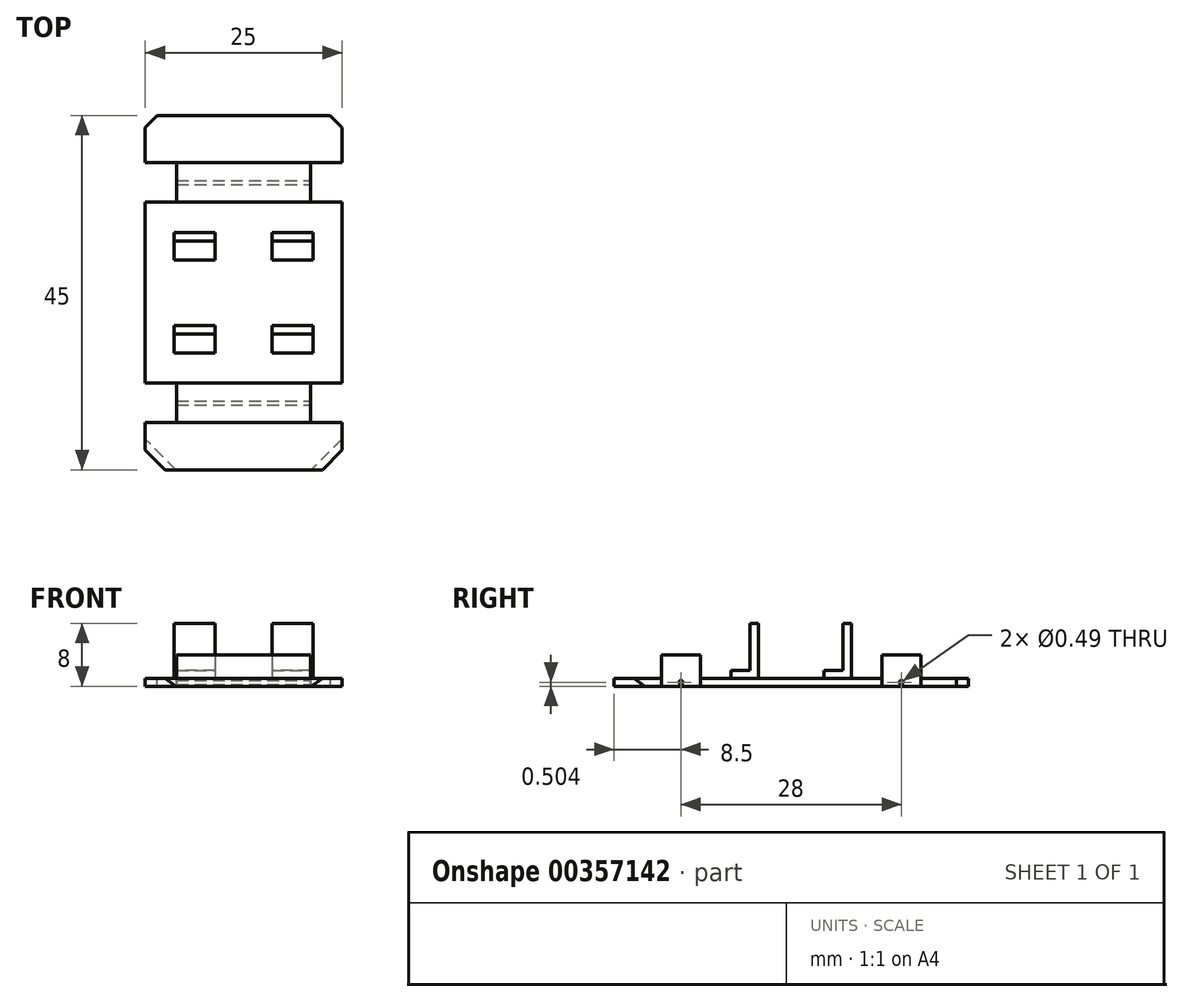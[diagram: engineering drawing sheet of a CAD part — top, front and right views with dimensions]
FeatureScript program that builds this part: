
annotation { "Feature Type Name" : "Feature", "Feature Type Description" : "" }
export const myFeature = defineFeature(function(context is Context, id is Id, definition is map)
    precondition{}
    {
        {
            var Q0;
            Q0=qCreatedBy(makeId("Top.planeOp"),FACE);
            var sketch = newSketch(context, id + "F0", { "sketchPlane" : qUnion([Q0])});
            skLineSegment(sketch, "E0.bottom", {"start": v(12.5, -22.5) * mm, "end": v(-12.5, -22.5) * mm});
            skLineSegment(sketch, "E0.top", {"start": v(12.5, 22.5) * mm, "end": v(-12.5, 22.5) * mm});
            skLineSegment(sketch, "E0.left", {"start": v(12.5, -22.5) * mm, "end": v(12.5, -16.5) * mm});
            skLineSegment(sketch, "E0.right", {"start": v(-12.5, -22.5) * mm, "end": v(-12.5, -16.5) * mm});
            skPoint(sketch, "E0.middle", {"position": v(0, 0) * mm});
            skLineSegment(sketch, "E1.bottom", {"start": v(-12.5, 16.5) * mm, "end": v(-8.5, 16.5) * mm});
            skLineSegment(sketch, "E1.top", {"start": v(-12.5, 11.5) * mm, "end": v(-8.5, 11.5) * mm});
            skLineSegment(sketch, "E1.right", {"start": v(-8.5, 16.5) * mm, "end": v(-8.5, 11.5) * mm});
            skLineSegment(sketch, "E2.MirrorCS", {"start": v(8.5, 16.5) * mm, "end": v(8.5, 11.5) * mm});
            skLineSegment(sketch, "E3.MirrorCS", {"start": v(12.5, 16.5) * mm, "end": v(8.5, 16.5) * mm});
            skLineSegment(sketch, "E4.MirrorCS", {"start": v(12.5, 11.5) * mm, "end": v(8.5, 11.5) * mm});
            skLineSegment(sketch, "E5.MirrorCS", {"start": v(12.5, -11.5) * mm, "end": v(8.5, -11.5) * mm});
            skLineSegment(sketch, "E6.MirrorCS", {"start": v(8.5, -16.5) * mm, "end": v(8.5, -11.5) * mm});
            skLineSegment(sketch, "E7.MirrorCS", {"start": v(12.5, -16.5) * mm, "end": v(8.5, -16.5) * mm});
            skLineSegment(sketch, "E8.MirrorCS", {"start": v(-12.5, -11.5) * mm, "end": v(-8.5, -11.5) * mm});
            skLineSegment(sketch, "E9.MirrorCS", {"start": v(-8.5, -16.5) * mm, "end": v(-8.5, -11.5) * mm});
            skLineSegment(sketch, "E10.MirrorCS", {"start": v(-12.5, -16.5) * mm, "end": v(-8.5, -16.5) * mm});
            skLineSegment(sketch, "E11.trimOffspring", {"start": v(12.5, 16.5) * mm, "end": v(12.5, 22.5) * mm});
            skLineSegment(sketch, "E12.trimOffspring", {"start": v(-12.5, 16.5) * mm, "end": v(-12.5, 22.5) * mm});
            skLineSegment(sketch, "E13.trimOffspring", {"start": v(-12.5, -11.5) * mm, "end": v(-12.5, 11.5) * mm});
            skLineSegment(sketch, "E14.trimOffspring", {"start": v(12.5, -11.5) * mm, "end": v(12.5, 11.5) * mm});
            skSolve(sketch);
        }
        {
            var Q0;
            Q0 = qSketchRegion(id + "F0", true);
            extrude(context, id + "F1", {"entities" : qUnion([Q0]), "depth" : 1 * mm});
        }
        {
            var Q0;
            Q0=qCreatedBy(makeId("Right.planeOp"),FACE);
            var sketch = newSketch(context, id + "F2", { "sketchPlane" : qUnion([Q0])});
            skLineSegment(sketch, "E15", {"start": v(-16.5, 1) * mm, "end": v(-11.5, 1) * mm});
            skPoint(sketch, "E16.centerSnap0", {"position": v(-14, 1) * mm});
            skLineSegment(sketch, "E17.MirrorCS", {"start": v(16.5, 1) * mm, "end": v(11.5, 1) * mm});
            skLineSegment(sketch, "E18.top", {"start": v(-16.5, 4) * mm, "end": v(-11.5, 4) * mm});
            skLineSegment(sketch, "E18.left", {"start": v(-16.5, 1) * mm, "end": v(-16.5, 4) * mm});
            skLineSegment(sketch, "E18.right", {"start": v(-11.5, 1) * mm, "end": v(-11.5, 4) * mm});
            skLineSegment(sketch, "E19.bottom", {"start": v(11.5, 1) * mm, "end": v(16.5, 1) * mm});
            skLineSegment(sketch, "E19.top", {"start": v(11.5, 4) * mm, "end": v(16.5, 4) * mm});
            skLineSegment(sketch, "E19.left", {"start": v(11.5, 1) * mm, "end": v(11.5, 4) * mm});
            skLineSegment(sketch, "E19.right", {"start": v(16.5, 1) * mm, "end": v(16.5, 4) * mm});
            skPoint(sketch, "E20.centerSnap0", {"position": v(14, 1) * mm});
            skSolve(sketch);
        }
        {
            var Q0;
            Q0 = qSketchRegion(id + "F2", true);
            extrude(context, id + "F3", {"entities" : qUnion([Q0]), "operationType" : NewBodyOperationType.ADD, "endBound" : BoundingType.SYMMETRIC, "depth" : 17 * mm});
        }
        {
            var Q0;
            Q0=makeQuery(id+"F1.opExtrude","SWEPT_EDGE",EDGE,{"disambiguationData":[OSD([sQuery(id+"F0.wireOp",EDGE,"E0.bottom"),sQuery(id+"F0.wireOp",EDGE,"E0.left")])]});
            var Q1;
            Q1=makeQuery(id+"F1.opExtrude","SWEPT_EDGE",EDGE,{"disambiguationData":[OSD([sQuery(id+"F0.wireOp",EDGE,"E0.bottom"),sQuery(id+"F0.wireOp",EDGE,"E0.right")])]});
            chamfer(context, id + "F4", {"entities" : qUnion([Q0, Q1]), "width" : 2.5 * mm, "tangentPropagation" : true});
        }
        {
            var Q0;
            Q0=makeQuery(id+"F1.opExtrude","SWEPT_EDGE",EDGE,{"disambiguationData":[OSD([sQuery(id+"F0.wireOp",EDGE,"E0.top"),sQuery(id+"F0.wireOp",EDGE,"E11.trimOffspring")])]});
            var Q1;
            Q1=makeQuery(id+"F1.opExtrude","SWEPT_EDGE",EDGE,{"disambiguationData":[OSD([sQuery(id+"F0.wireOp",EDGE,"E0.top"),sQuery(id+"F0.wireOp",EDGE,"E12.trimOffspring")])]});
            chamfer(context, id + "F5", {"entities" : qUnion([Q0, Q1]), "width" : 1.5 * mm, "tangentPropagation" : true});
        }
        {
            var Q0;
            {var subQ0=sQuery(id+"F0.wireOp",EDGE,"E0.right");var subQ1=sQuery(id+"F0.wireOp",EDGE,"E0.bottom");Q0=makeQuery(id+"F4.opChamfer","BLEND_EDGE",EDGE,{"blendedFrom":[makeQuery(id+"F1.opExtrude","SWEPT_EDGE",EDGE,{"disambiguationData":[OSD([subQ1,subQ0])]}),makeQuery(id+"F1.opExtrude","CAP_FACE",FACE,{"disambiguationData":[OSD([subQ1,sQuery(id+"F0.wireOp",EDGE,"E0.top"),sQuery(id+"F0.wireOp",EDGE,"E0.left"),subQ0,sQuery(id+"F0.wireOp",EDGE,"E1.bottom"),sQuery(id+"F0.wireOp",EDGE,"E1.top"),sQuery(id+"F0.wireOp",EDGE,"E1.right"),sQuery(id+"F0.wireOp",EDGE,"E2.MirrorCS"),sQuery(id+"F0.wireOp",EDGE,"E3.MirrorCS"),sQuery(id+"F0.wireOp",EDGE,"E4.MirrorCS"),sQuery(id+"F0.wireOp",EDGE,"E5.MirrorCS"),sQuery(id+"F0.wireOp",EDGE,"E6.MirrorCS"),sQuery(id+"F0.wireOp",EDGE,"E7.MirrorCS"),sQuery(id+"F0.wireOp",EDGE,"E8.MirrorCS"),sQuery(id+"F0.wireOp",EDGE,"E9.MirrorCS"),sQuery(id+"F0.wireOp",EDGE,"E10.MirrorCS"),sQuery(id+"F0.wireOp",EDGE,"E11.trimOffspring"),sQuery(id+"F0.wireOp",EDGE,"E12.trimOffspring"),sQuery(id+"F0.wireOp",EDGE,"E13.trimOffspring"),sQuery(id+"F0.wireOp",EDGE,"E14.trimOffspring")])],"isStart":true})],"blendedInto":[makeQuery(id+"F1.opExtrude","CAP_FACE",FACE,{"disambiguationData":[OSD([subQ1,sQuery(id+"F0.wireOp",EDGE,"E0.top"),sQuery(id+"F0.wireOp",EDGE,"E0.left"),subQ0,sQuery(id+"F0.wireOp",EDGE,"E1.bottom"),sQuery(id+"F0.wireOp",EDGE,"E1.top"),sQuery(id+"F0.wireOp",EDGE,"E1.right"),sQuery(id+"F0.wireOp",EDGE,"E2.MirrorCS"),sQuery(id+"F0.wireOp",EDGE,"E3.MirrorCS"),sQuery(id+"F0.wireOp",EDGE,"E4.MirrorCS"),sQuery(id+"F0.wireOp",EDGE,"E5.MirrorCS"),sQuery(id+"F0.wireOp",EDGE,"E6.MirrorCS"),sQuery(id+"F0.wireOp",EDGE,"E7.MirrorCS"),sQuery(id+"F0.wireOp",EDGE,"E8.MirrorCS"),sQuery(id+"F0.wireOp",EDGE,"E9.MirrorCS"),sQuery(id+"F0.wireOp",EDGE,"E10.MirrorCS"),sQuery(id+"F0.wireOp",EDGE,"E11.trimOffspring"),sQuery(id+"F0.wireOp",EDGE,"E12.trimOffspring"),sQuery(id+"F0.wireOp",EDGE,"E13.trimOffspring"),sQuery(id+"F0.wireOp",EDGE,"E14.trimOffspring")])],"isStart":true})]});}
            var Q1;
            {var subQ0=sQuery(id+"F0.wireOp",EDGE,"E0.left");var subQ1=sQuery(id+"F0.wireOp",EDGE,"E0.bottom");Q1=makeQuery(id+"F4.opChamfer","BLEND_EDGE",EDGE,{"blendedFrom":[makeQuery(id+"F1.opExtrude","SWEPT_EDGE",EDGE,{"disambiguationData":[OSD([subQ1,subQ0])]}),makeQuery(id+"F1.opExtrude","CAP_FACE",FACE,{"disambiguationData":[OSD([subQ1,sQuery(id+"F0.wireOp",EDGE,"E0.top"),subQ0,sQuery(id+"F0.wireOp",EDGE,"E0.right"),sQuery(id+"F0.wireOp",EDGE,"E1.bottom"),sQuery(id+"F0.wireOp",EDGE,"E1.top"),sQuery(id+"F0.wireOp",EDGE,"E1.right"),sQuery(id+"F0.wireOp",EDGE,"E2.MirrorCS"),sQuery(id+"F0.wireOp",EDGE,"E3.MirrorCS"),sQuery(id+"F0.wireOp",EDGE,"E4.MirrorCS"),sQuery(id+"F0.wireOp",EDGE,"E5.MirrorCS"),sQuery(id+"F0.wireOp",EDGE,"E6.MirrorCS"),sQuery(id+"F0.wireOp",EDGE,"E7.MirrorCS"),sQuery(id+"F0.wireOp",EDGE,"E8.MirrorCS"),sQuery(id+"F0.wireOp",EDGE,"E9.MirrorCS"),sQuery(id+"F0.wireOp",EDGE,"E10.MirrorCS"),sQuery(id+"F0.wireOp",EDGE,"E11.trimOffspring"),sQuery(id+"F0.wireOp",EDGE,"E12.trimOffspring"),sQuery(id+"F0.wireOp",EDGE,"E13.trimOffspring"),sQuery(id+"F0.wireOp",EDGE,"E14.trimOffspring")])],"isStart":true})],"blendedInto":[makeQuery(id+"F1.opExtrude","CAP_FACE",FACE,{"disambiguationData":[OSD([subQ1,sQuery(id+"F0.wireOp",EDGE,"E0.top"),subQ0,sQuery(id+"F0.wireOp",EDGE,"E0.right"),sQuery(id+"F0.wireOp",EDGE,"E1.bottom"),sQuery(id+"F0.wireOp",EDGE,"E1.top"),sQuery(id+"F0.wireOp",EDGE,"E1.right"),sQuery(id+"F0.wireOp",EDGE,"E2.MirrorCS"),sQuery(id+"F0.wireOp",EDGE,"E3.MirrorCS"),sQuery(id+"F0.wireOp",EDGE,"E4.MirrorCS"),sQuery(id+"F0.wireOp",EDGE,"E5.MirrorCS"),sQuery(id+"F0.wireOp",EDGE,"E6.MirrorCS"),sQuery(id+"F0.wireOp",EDGE,"E7.MirrorCS"),sQuery(id+"F0.wireOp",EDGE,"E8.MirrorCS"),sQuery(id+"F0.wireOp",EDGE,"E9.MirrorCS"),sQuery(id+"F0.wireOp",EDGE,"E10.MirrorCS"),sQuery(id+"F0.wireOp",EDGE,"E11.trimOffspring"),sQuery(id+"F0.wireOp",EDGE,"E12.trimOffspring"),sQuery(id+"F0.wireOp",EDGE,"E13.trimOffspring"),sQuery(id+"F0.wireOp",EDGE,"E14.trimOffspring")])],"isStart":true})]});}
            chamfer(context, id + "F6", {"entities" : qUnion([Q0, Q1]), "width" : 1 * mm, "tangentPropagation" : true});
        }
        {
            var Q0;
            Q0=makeQuery(id+"F3.boolean.opBoolean","MERGE",FACE,{"derivedFrom":[makeQuery(id+"F1.opExtrude","SWEPT_FACE",FACE,{"disambiguationData":[OSD([sQuery(id+"F0.wireOp",EDGE,"E6.MirrorCS")])]}),makeQuery(id+"F3.opExtrude","CAP_FACE",FACE,{"disambiguationData":[OSD([sQuery(id+"F2.wireOp",EDGE,"E15"),sQuery(id+"F2.wireOp",EDGE,"E18.top"),sQuery(id+"F2.wireOp",EDGE,"E18.left"),sQuery(id+"F2.wireOp",EDGE,"E18.right")])],"isStart":false})]});
            var sketch = newSketch(context, id + "F7", { "sketchPlane" : qUnion([Q0])});
            skCircle(sketch, "E21", {"center": v(-14, 0.5) * mm, "radius": 0.24 * mm});
            skPoint(sketch, "E21.centerSnap0", {"position": v(-14, 0) * mm});
            skCircle(sketch, "E22.MirrorC", {"center": v(14, 0.5) * mm, "radius": 0.24 * mm});
            skSolve(sketch);
        }
        {
            var Q0;
            Q0 = qSketchRegion(id + "F7", true);
            extrude(context, id + "F8", {"entities" : qUnion([Q0]), "operationType" : NewBodyOperationType.REMOVE, "oppositeDirection" : true, "depth" : 17 * mm});
        }
        {
            var Q0;
            {var subQ0=sQuery(id+"F0.wireOp",EDGE,"E14.trimOffspring");var subQ1=sQuery(id+"F0.wireOp",EDGE,"E9.MirrorCS");var subQ2=sQuery(id+"F0.wireOp",EDGE,"E8.MirrorCS");var subQ3=sQuery(id+"F0.wireOp",EDGE,"E6.MirrorCS");var subQ4=sQuery(id+"F0.wireOp",EDGE,"E5.MirrorCS");var subQ9=sQuery(id+"F0.wireOp",EDGE,"E1.top");var subQ10=sQuery(id+"F0.wireOp",EDGE,"E1.right");var subQ11=sQuery(id+"F0.wireOp",EDGE,"E13.trimOffspring");var subQ12=sQuery(id+"F0.wireOp",EDGE,"E2.MirrorCS");var subQ14=sQuery(id+"F0.wireOp",EDGE,"E4.MirrorCS");Q0=makeQuery(id+"F3.boolean.opBoolean","SPLIT",FACE,{"disambiguationData":[TD([makeQuery(id+"F1.opExtrude","SWEPT_FACE",FACE,{"disambiguationData":[OSD([subQ9])]})])],"derivedFrom":makeQuery(id+"F1.opExtrude","CAP_FACE",FACE,{"disambiguationData":[OSD([sQuery(id+"F0.wireOp",EDGE,"E0.bottom"),sQuery(id+"F0.wireOp",EDGE,"E0.top"),sQuery(id+"F0.wireOp",EDGE,"E0.left"),sQuery(id+"F0.wireOp",EDGE,"E0.right"),sQuery(id+"F0.wireOp",EDGE,"E1.bottom"),subQ9,subQ10,subQ12,sQuery(id+"F0.wireOp",EDGE,"E3.MirrorCS"),subQ14,subQ4,subQ3,sQuery(id+"F0.wireOp",EDGE,"E7.MirrorCS"),subQ2,subQ1,sQuery(id+"F0.wireOp",EDGE,"E10.MirrorCS"),sQuery(id+"F0.wireOp",EDGE,"E11.trimOffspring"),sQuery(id+"F0.wireOp",EDGE,"E12.trimOffspring"),subQ11,subQ0])],"isStart":false})});}
            var sketch = newSketch(context, id + "F9", { "sketchPlane" : qUnion([Q0])});
            skLineSegment(sketch, "E23.bottom", {"start": v(8.83, -7.65) * mm, "end": v(3.63, -7.65) * mm});
            skLineSegment(sketch, "E23.top", {"start": v(8.83, -4.15) * mm, "end": v(3.63, -4.15) * mm});
            skLineSegment(sketch, "E23.left", {"start": v(8.83, -7.65) * mm, "end": v(8.83, -4.15) * mm});
            skLineSegment(sketch, "E23.right", {"start": v(3.63, -7.65) * mm, "end": v(3.63, -4.15) * mm});
            skLineSegment(sketch, "E24.MirrorCS", {"start": v(-8.83, -4.15) * mm, "end": v(-3.63, -4.15) * mm});
            skLineSegment(sketch, "E25.MirrorCS", {"start": v(-3.63, -7.65) * mm, "end": v(-3.63, -4.15) * mm});
            skLineSegment(sketch, "E26.MirrorCS", {"start": v(-8.83, -7.65) * mm, "end": v(-3.63, -7.65) * mm});
            skLineSegment(sketch, "E27.MirrorCS", {"start": v(-8.83, -7.65) * mm, "end": v(-8.83, -4.15) * mm});
            skLineSegment(sketch, "E28.MirrorCS", {"start": v(-8.83, 4.15) * mm, "end": v(-3.63, 4.15) * mm});
            skLineSegment(sketch, "E29.MirrorCS", {"start": v(-3.63, 7.65) * mm, "end": v(-3.63, 4.15) * mm});
            skLineSegment(sketch, "E30.MirrorCS", {"start": v(-8.83, 7.65) * mm, "end": v(-3.63, 7.65) * mm});
            skLineSegment(sketch, "E31.MirrorCS", {"start": v(-8.83, 7.65) * mm, "end": v(-8.83, 4.15) * mm});
            skLineSegment(sketch, "E32.MirrorCS", {"start": v(8.83, 7.65) * mm, "end": v(3.63, 7.65) * mm});
            skLineSegment(sketch, "E33.MirrorCS", {"start": v(8.83, 7.65) * mm, "end": v(8.83, 4.15) * mm});
            skLineSegment(sketch, "E34.MirrorCS", {"start": v(8.83, 4.15) * mm, "end": v(3.63, 4.15) * mm});
            skLineSegment(sketch, "E35.MirrorCS", {"start": v(3.63, 7.65) * mm, "end": v(3.63, 4.15) * mm});
            skSolve(sketch);
        }
        {
            var Q0;
            Q0 = qSketchRegion(id + "F9", true);
            extrude(context, id + "F10", {"entities" : qUnion([Q0]), "operationType" : NewBodyOperationType.ADD, "depth" : 1 * mm});
        }
        {
            var Q0;
            Q0=makeQuery(id+"F10.opExtrude","CAP_FACE",FACE,{"disambiguationData":[OSD([sQuery(id+"F9.wireOp",EDGE,"E23.bottom"),sQuery(id+"F9.wireOp",EDGE,"E23.top"),sQuery(id+"F9.wireOp",EDGE,"E23.left"),sQuery(id+"F9.wireOp",EDGE,"E23.right")])],"isStart":false});
            var sketch = newSketch(context, id + "F11", { "sketchPlane" : qUnion([Q0])});
            skLineSegment(sketch, "E36.bottom", {"start": v(3.63, -4.15) * mm, "end": v(8.83, -4.15) * mm});
            skLineSegment(sketch, "E36.top", {"start": v(3.63, -5.23) * mm, "end": v(8.83, -5.23) * mm});
            skLineSegment(sketch, "E36.left", {"start": v(3.63, -4.15) * mm, "end": v(3.63, -5.23) * mm});
            skLineSegment(sketch, "E36.right", {"start": v(8.83, -4.15) * mm, "end": v(8.83, -5.23) * mm});
            skLineSegment(sketch, "E37.MirrorCS", {"start": v(-3.63, -4.15) * mm, "end": v(-8.83, -4.15) * mm});
            skLineSegment(sketch, "E38.MirrorCS", {"start": v(-3.63, -4.15) * mm, "end": v(-3.63, -5.23) * mm});
            skLineSegment(sketch, "E39.MirrorCS", {"start": v(-8.83, -4.15) * mm, "end": v(-8.83, -5.23) * mm});
            skLineSegment(sketch, "E40.MirrorCS", {"start": v(-3.63, -5.23) * mm, "end": v(-8.83, -5.23) * mm});
            skSolve(sketch);
        }
        {
            var Q0;
            Q0 = qSketchRegion(id + "F11", true);
            extrude(context, id + "F12", {"entities" : qUnion([Q0]), "operationType" : NewBodyOperationType.ADD, "depth" : 6 * mm});
        }
        {
            var Q0;
            Q0=makeQuery(id+"F10.opExtrude","CAP_FACE",FACE,{"disambiguationData":[OSD([sQuery(id+"F9.wireOp",EDGE,"E32.MirrorCS"),sQuery(id+"F9.wireOp",EDGE,"E33.MirrorCS"),sQuery(id+"F9.wireOp",EDGE,"E34.MirrorCS"),sQuery(id+"F9.wireOp",EDGE,"E35.MirrorCS")])],"isStart":false});
            var sketch = newSketch(context, id + "F13", { "sketchPlane" : qUnion([Q0])});
            skLineSegment(sketch, "E41.bottom", {"start": v(3.63, 7.65) * mm, "end": v(8.83, 7.65) * mm});
            skLineSegment(sketch, "E41.top", {"start": v(3.63, 6.57) * mm, "end": v(8.83, 6.57) * mm});
            skLineSegment(sketch, "E41.left", {"start": v(3.63, 7.65) * mm, "end": v(3.63, 6.57) * mm});
            skLineSegment(sketch, "E41.right", {"start": v(8.83, 7.65) * mm, "end": v(8.83, 6.57) * mm});
            skLineSegment(sketch, "E42.MirrorCS", {"start": v(-8.83, 7.65) * mm, "end": v(-8.83, 6.57) * mm});
            skLineSegment(sketch, "E43.MirrorCS", {"start": v(-3.63, 6.57) * mm, "end": v(-8.83, 6.57) * mm});
            skLineSegment(sketch, "E44.MirrorCS", {"start": v(-3.63, 7.65) * mm, "end": v(-8.83, 7.65) * mm});
            skLineSegment(sketch, "E45.MirrorCS", {"start": v(-3.63, 7.65) * mm, "end": v(-3.63, 6.57) * mm});
            skSolve(sketch);
        }
        {
            var Q0;
            Q0 = qSketchRegion(id + "F13", true);
            extrude(context, id + "F14", {"entities" : qUnion([Q0]), "operationType" : NewBodyOperationType.ADD, "depth" : 6 * mm});
        }
    });
